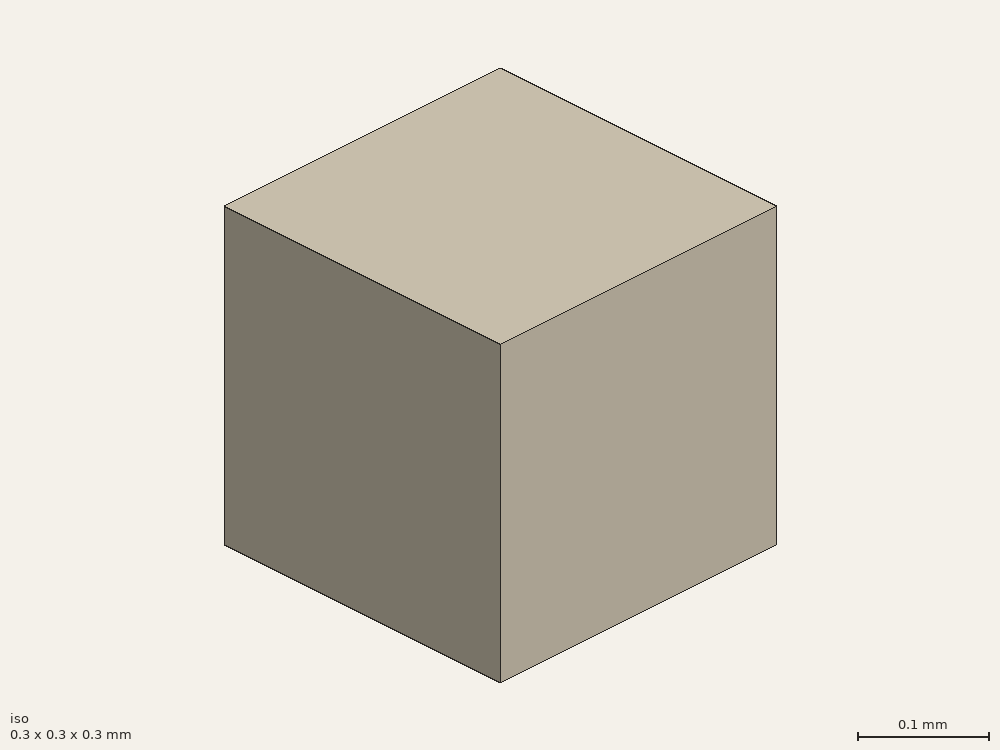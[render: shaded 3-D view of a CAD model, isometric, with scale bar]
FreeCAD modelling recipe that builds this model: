
FCSTD DOCUMENT  (FreeCAD 0.21R33694 (Git))
Label: patch
License: All rights reserved
LicenseURL: http://en.wikipedia.org/wiki/All_rights_reserved
objects: Part::Part2DObjectPython×20, Part::Cut×11, Part::Extrusion×10, App::FeaturePython×9, Part::FeaturePython×6
note: 47 computed .brp shape members not serialized (recipe doc carries the construction recipe); baked Part::Feature solids carry a one-line shape summary decoded from their .brp

FEATURE [Part::Part2DObjectPython] Rectangle  label="gp2D"  # Draft 2D object (typed FeaturePython)
  Area = 6400
  ChamferSize = 0
  Columns = 1
  FilletRadius = 0
  Height = 80
  Length = 80
  MakeFace = true
  Placement = pos=(-75,-75,0) rot=(0,0,1;0rad)
  Rows = 1
FEATURE [Part::Part2DObjectPython] Polygon  label="inner2D"  # Draft 2D object (typed FeaturePython)
  Area = 1.10213
  ChamferSize = 0
  DrawMode = 0
  FacesNumber = 16
  FilletRadius = 0
  MakeFace = true
  Radius = 0.6
FEATURE [Part::Part2DObjectPython] Polygon001  label="outer2D"  # Draft 2D object (typed FeaturePython)
  Area = 13.1181
  ChamferSize = 0
  DrawMode = 0
  FacesNumber = 16
  FilletRadius = 0
  MakeFace = true
  Radius = 2.07
FEATURE [Part::Part2DObjectPython] Polygon002  label="barrel2D"  # Draft 2D object (typed FeaturePython)
  Area = 27.5532
  ChamferSize = 0
  DrawMode = 0
  FacesNumber = 16
  FilletRadius = 0
  MakeFace = true
  Radius = 3
FEATURE [Part::Part2DObjectPython] Clone2D  label="inner2D (2D)"  # Draft 2D object (typed FeaturePython)
  Fuse = false
  Objects = -> [Polygon]
  Scale = (1,1,1)
FEATURE [Part::Extrusion] Extrude001  label="coax-pin"
  Base = -> Clone2D
  Dir = (0,0,1)
  DirMode = 2
  FaceMakerClass = Part::FaceMakerBullseye
  LengthFwd = -1
  LengthRev = 0
  Solid = false
  Symmetric = false
FEATURE [Part::Extrusion] Extrude002  label="coax-dielectic"
  Base = -> Polygon001
  Dir = (0,0,1)
  DirMode = 2
  FaceMakerClass = Part::FaceMakerBullseye
  LengthFwd = -1
  LengthRev = 0
  Solid = false
  Symmetric = false
FEATURE [Part::Extrusion] Extrude003  label="coax-outer"
  Base = -> Polygon002
  Dir = (0,0,1)
  DirMode = 2
  FaceMakerClass = Part::FaceMakerBullseye
  LengthFwd = -2
  LengthRev = 0
  Solid = false
  Symmetric = false
FEATURE [Part::Cut] Cut001  label="teflon"
  Base = -> Extrude002
  Tool = -> Extrude001
FEATURE [Part::Extrusion] Extrude004
  Base = -> Rectangle
  Dir = (0,0,1)
  DirMode = 2
  FaceMakerClass = Part::FaceMakerBullseye
  LengthFwd = -0.2
  LengthRev = 0
  Placement = pos=(35,35,0) rot=(0,0,1;0rad)
  Solid = false
  Symmetric = false
FEATURE [Part::Part2DObjectPython] Clone2D001  label="barrel2D (2D)"  # Draft 2D object (typed FeaturePython)
  Fuse = false
  Objects = -> [Polygon002]
  Scale = (1,1,1)
FEATURE [Part::Extrusion] Extrude005
  Base = -> Clone2D001
  Dir = (0,0,1)
  DirMode = 2
  FaceMakerClass = Part::FaceMakerBullseye
  LengthFwd = -5
  LengthRev = 0
  Solid = false
  Symmetric = false
FEATURE [Part::Part2DObjectPython] Rectangle003  label="air2D"  # Draft 2D object (typed FeaturePython)
  Area = 90000
  ChamferSize = 0
  Columns = 1
  FilletRadius = 0
  Height = 300
  Length = 300
  MakeFace = true
  Placement = pos=(-150,-150,0) rot=(0,0,1;0rad)
  Rows = 1
FEATURE [Part::Part2DObjectPython] Wire  label="_Pport"  # Draft 2D object (typed FeaturePython)
  Area = 1.31181e-05
  ChamferSize = 0
  Closed = true
  End = (0,-0.00207,-0.001)
  FilletRadius = 0
  Length = 0.0129228
  MakeFace = true
  Placement = pos=(0.000792155,-0.00191243,-0.001) rot=(0,0,1;0rad)
  Points = (16) [(0,0,0),(0.000671556,0.00044872,0),(0.00112028,0.00112028,0),(0.00127785,0.00191243,0),(0.00112028,0.00270459,0),(0.000671556,0.00337614,0),+10 more]
  Start = (0.000792155,-0.00191243,-0.001)
  Subdivisions = 0
FEATURE [Part::Part2DObjectPython] Wire001  label="_Pi"  # Draft 2D object (typed FeaturePython)
  Area = 1.10213e-06
  ChamferSize = 0
  Closed = true
  End = (0.00022961,-0.000554328,-0.001)
  FilletRadius = 0
  Length = 0.00374573
  MakeFace = true
  Placement = pos=(0.000424264,-0.000424264,-0.001) rot=(0,0,1;0rad)
  Points = (16) [(0,0,0),(0.000130064,0.000194654,0),(0.000175736,0.000424264,0),(0.000130064,0.000653874,0),(0,0.000848528,0),(-0.000194654,0.000978592,0),+10 more]
  Start = (0.000424264,-0.000424264,-0.001)
  Subdivisions = 0
FEATURE [Part::Part2DObjectPython] Line  label="_Pv"  # Draft 2D object (typed FeaturePython)
  Area = 0
  ChamferSize = 0
  Closed = false
  End = (0.000424264,-0.000424264,-0.001)
  FilletRadius = 0
  Length = 0.00147
  MakeFace = true
  Placement = pos=(0.00146371,-0.00146371,-0.001) rot=(0,0,1;0rad)
  Points = (2) [(0,0,0),(-0.00103945,0.00103945,0)]
  Start = (0.00146371,-0.00146371,-0.001)
  Subdivisions = 0
FEATURE [App::FeaturePython] Text  label="_Btop(radiation){top}"  # WARN: FeaturePython — macro-defined, semantics opaque (R4)
  Placement = pos=(0.308621,-0.303467,0.318) rot=(0,0,1;0rad)
  Text = .
FEATURE [App::FeaturePython] Text001  label="_Bfront(radiation){front}"  # WARN: FeaturePython — macro-defined, semantics opaque (R4)
  Placement = pos=(0.308621,-0.303467,0.3) rot=(0,0,1;0rad)
  Text = .
FEATURE [App::FeaturePython] Text002  label="_Bright(radiation){right}"  # WARN: FeaturePython — macro-defined, semantics opaque (R4)
  Placement = pos=(0.308621,-0.303467,0.3) rot=(0,0,1;0rad)
  Text = .
FEATURE [App::FeaturePython] Text003  label="_Bleft(radiation){left}"  # WARN: FeaturePython — macro-defined, semantics opaque (R4)
  Placement = pos=(0.308621,-0.303467,0.3) rot=(0,0,1;0rad)
  Text = .
FEATURE [App::FeaturePython] Text004  label="_Bback(radiation){back}"  # WARN: FeaturePython — macro-defined, semantics opaque (R4)
  Placement = pos=(0.308621,-0.303467,0.3) rot=(0,0,1;0rad)
  Text = .
FEATURE [App::FeaturePython] Text005  label="_Bbottom(radiation){bottom}"  # WARN: FeaturePython — macro-defined, semantics opaque (R4)
  Placement = pos=(0.308621,-0.303467,0.3) rot=(0,0,1;0rad)
  Text = .
FEATURE [App::FeaturePython] Text006  label="_Sin(PV){port}"  # WARN: FeaturePython — macro-defined, semantics opaque (R4)
  Placement = pos=(0.308621,-0.303467,0.3) rot=(0,0,1;0rad)
  Text = .
FEATURE [App::FeaturePython] Text007  label="_Min(1,voltage){v}"  # WARN: FeaturePython — macro-defined, semantics opaque (R4)
  Placement = pos=(0.308621,-0.303467,0.3) rot=(0,0,1;0rad)
  Text = .
FEATURE [App::FeaturePython] Text008  label="_Min(1,current){i}"  # WARN: FeaturePython — macro-defined, semantics opaque (R4)
  Placement = pos=(0.308621,-0.303467,0.3) rot=(0,0,1;0rad)
  Text = .
FEATURE [Part::Extrusion] Extrude  label="air"
  Base = -> Rectangle003
  Dir = (0,0,1)
  DirMode = 2
  FaceMakerClass = Part::FaceMakerBullseye
  LengthFwd = 300
  LengthRev = 0
  Placement = pos=(0,0,-110) rot=(0,0,1;0rad)
  Solid = false
  Symmetric = false
FEATURE [Part::Part2DObjectPython] Rectangle014  label="_Pfront"  # Draft 2D object (typed FeaturePython)
  Area = 0.09
  ChamferSize = 0
  Columns = 1
  FilletRadius = 0
  Height = 0.3
  Length = 0.3
  MakeFace = true
  Placement = pos=(-0.15,-0.15,-0.11) rot=(1,0,0;1.5708rad)
  Rows = 1
FEATURE [Part::Part2DObjectPython] Rectangle015  label="_Pback"  # Draft 2D object (typed FeaturePython)
  Area = 0.09
  ChamferSize = 0
  Columns = 1
  FilletRadius = 0
  Height = 0.3
  Length = 0.3
  MakeFace = true
  Placement = pos=(-0.15,0.15,-0.11) rot=(1,0,0;1.5708rad)
  Rows = 1
FEATURE [Part::Part2DObjectPython] Rectangle016  label="_Ptop"  # Draft 2D object (typed FeaturePython)
  Area = 0.09
  ChamferSize = 0
  Columns = 1
  FilletRadius = 0
  Height = 0.3
  Length = 0.3
  MakeFace = true
  Placement = pos=(-0.15,-0.15,0.19) rot=(0,0,1;0rad)
  Rows = 1
FEATURE [Part::Part2DObjectPython] Rectangle017  label="_Pbottom"  # Draft 2D object (typed FeaturePython)
  Area = 0.09
  ChamferSize = 0
  Columns = 1
  FilletRadius = 0
  Height = 0.3
  Length = 0.3
  MakeFace = true
  Placement = pos=(-0.15,-0.15,-0.11) rot=(0,0,1;0rad)
  Rows = 1
FEATURE [Part::Part2DObjectPython] Rectangle018  label="_Pright"  # Draft 2D object (typed FeaturePython)
  Area = 0.09
  ChamferSize = 0
  Columns = 1
  FilletRadius = 0
  Height = 0.3
  Length = 0.3
  MakeFace = true
  Placement = pos=(0.15,-0.15,-0.11) rot=(0.57735,0.57735,0.57735;2.0944rad)
  Rows = 1
FEATURE [Part::Part2DObjectPython] Rectangle019  label="_Pleft"  # Draft 2D object (typed FeaturePython)
  Area = 0.09
  ChamferSize = 0
  Columns = 1
  FilletRadius = 0
  Height = 0.3
  Length = 0.3
  MakeFace = true
  Placement = pos=(-0.15,-0.15,-0.11) rot=(0.57735,0.57735,0.57735;2.0944rad)
  Rows = 1
FEATURE [Part::Part2DObjectPython] Rectangle020  # Draft 2D object (typed FeaturePython)
  Area = 6400
  ChamferSize = 0
  Columns = 1
  FilletRadius = 0
  Height = 80
  Length = 80
  MakeFace = true
  Placement = pos=(-39.8487,-39.8487,0) rot=(0,0,1;0rad)
  Rows = 1
FEATURE [Part::Extrusion] Extrude006  label="substrate_whole"
  Base = -> Rectangle020
  Dir = (0,0,1)
  DirMode = 2
  FaceMakerClass = Part::FaceMakerBullseye
  LengthFwd = 1
  LengthRev = 0
  Placement = pos=(-0.151333,-0.151333,0) rot=(0,0,1;0rad)
  Solid = false
  Symmetric = false
FEATURE [Part::Part2DObjectPython] Rectangle021  # Draft 2D object (typed FeaturePython)
  Area = 1183.36
  ChamferSize = 0
  Columns = 1
  FilletRadius = 0
  Height = 34.4
  Length = 34.4
  MakeFace = true
  Placement = pos=(-17.0487,-17.0487,1) rot=(0,0,1;0rad)
  Rows = 1
FEATURE [Part::Extrusion] Extrude007  label="patch"
  Base = -> Rectangle021
  Dir = (0,0,1)
  DirMode = 2
  FaceMakerClass = Part::FaceMakerBullseye
  LengthFwd = 0.02
  LengthRev = 0
  Placement = pos=(-0.151333,-0.151333,0) rot=(0,0,1;0rad)
  Solid = false
  Symmetric = false
FEATURE [Part::Part2DObjectPython] Polygon003  # Draft 2D object (typed FeaturePython)
  Area = 0.48
  ChamferSize = 0
  DrawMode = 0
  FacesNumber = 12
  FilletRadius = 0
  MakeFace = true
  Placement = pos=(-39.8487,-39.8487,0) rot=(0,0,1;0rad)
  Radius = 0.4
FEATURE [Part::Extrusion] Extrude008
  Base = -> Polygon003
  Dir = (0,0,1)
  DirMode = 2
  FaceMakerClass = Part::FaceMakerBullseye
  LengthFwd = 1
  LengthRev = 0
  Placement = pos=(39.8487,39.8487,0) rot=(0,0,1;0rad)
  Solid = false
  Symmetric = false
FEATURE [Part::Part2DObjectPython] Polygon004  # Draft 2D object (typed FeaturePython)
  Area = 1.08
  ChamferSize = 0
  DrawMode = 0
  FacesNumber = 12
  FilletRadius = 0
  MakeFace = true
  Placement = pos=(-39.8487,-39.8487,0) rot=(0,0,1;0rad)
  Radius = 0.6
FEATURE [Part::Extrusion] Extrude009
  Base = -> Polygon004
  Dir = (0,0,1)
  DirMode = 2
  FaceMakerClass = Part::FaceMakerBullseye
  LengthFwd = 1
  LengthRev = 0
  Placement = pos=(28.8487,28.8487,0) rot=(0,0,1;0rad)
  Solid = false
  Symmetric = false
FEATURE [Part::FeaturePython] Clone  label="Extrude010"  # Draft clone (typed FeaturePython)
  AttacherType = Attacher::AttachEngine3D
  Fuse = false
  Objects = -> [Extrude009]
  Placement = pos=(50.8487,28.8487,0) rot=(0,0,1;0rad)
  Scale = (1,1,1)
FEATURE [Part::FeaturePython] Clone001  label="Extrude011"  # Draft clone (typed FeaturePython)
  AttacherType = Attacher::AttachEngine3D
  Fuse = false
  Objects = -> [Extrude009]
  Placement = pos=(28.8487,50.8487,0) rot=(0,0,1;0rad)
  Scale = (1,1,1)
FEATURE [Part::FeaturePython] Clone002  label="Extrude012"  # Draft clone (typed FeaturePython)
  AttacherType = Attacher::AttachEngine3D
  Fuse = false
  Objects = -> [Clone001]
  Placement = pos=(50.8487,50.8487,0) rot=(0,0,1;0rad)
  Scale = (1,1,1)
FEATURE [Part::Cut] Cut007  label="gp"
  Base = -> Extrude004
  Tool = -> Extrude005
FEATURE [Part::Cut] Cut
  Base = -> Extrude006
  Tool = -> Extrude008
FEATURE [Part::Cut] Cut008
  Base = -> Cut
  Tool = -> Extrude009
FEATURE [Part::Cut] Cut009
  Base = -> Cut008
  Tool = -> Clone
FEATURE [Part::Cut] Cut010
  Base = -> Cut009
  Tool = -> Clone001
FEATURE [Part::Cut] Cut011  label="substrate"
  Base = -> Cut010
  Tool = -> Clone002
FEATURE [Part::FeaturePython] Clone003  label="substrate_void"  # Draft clone (typed FeaturePython)
  AttacherType = Attacher::AttachEngine3D
  Fuse = false
  Objects = -> [Extrude006]
  Placement = pos=(-0.151333,-0.151333,0) rot=(0,0,1;0rad)
  Scale = (1,1,1)
FEATURE [Part::Cut] Cut012
  Base = -> Extrude
  Tool = -> Extrude003
FEATURE [Part::Cut] Cut013
  Base = -> Cut012
  Tool = -> Clone003
FEATURE [Part::Cut] Cut014
  Base = -> Cut013
  Tool = -> Cut007
FEATURE [Part::Cut] Cut015
  Base = -> Cut014
  Tool = -> Extrude007
FEATURE [Part::FeaturePython] BooleanFragments  # WARN: FeaturePython — macro-defined, semantics opaque (R4)
  Mode = 0
  Objects = -> [Cut015,Cut011,Cut001]
  Tolerance = 0
FEATURE [Part::FeaturePython] Clone004  label="scaled"  # Draft clone (typed FeaturePython)
  AttacherType = Attacher::AttachEngine3D
  Fuse = false
  Objects = -> [BooleanFragments]
  Scale = (0.001,0.001,0.001)
